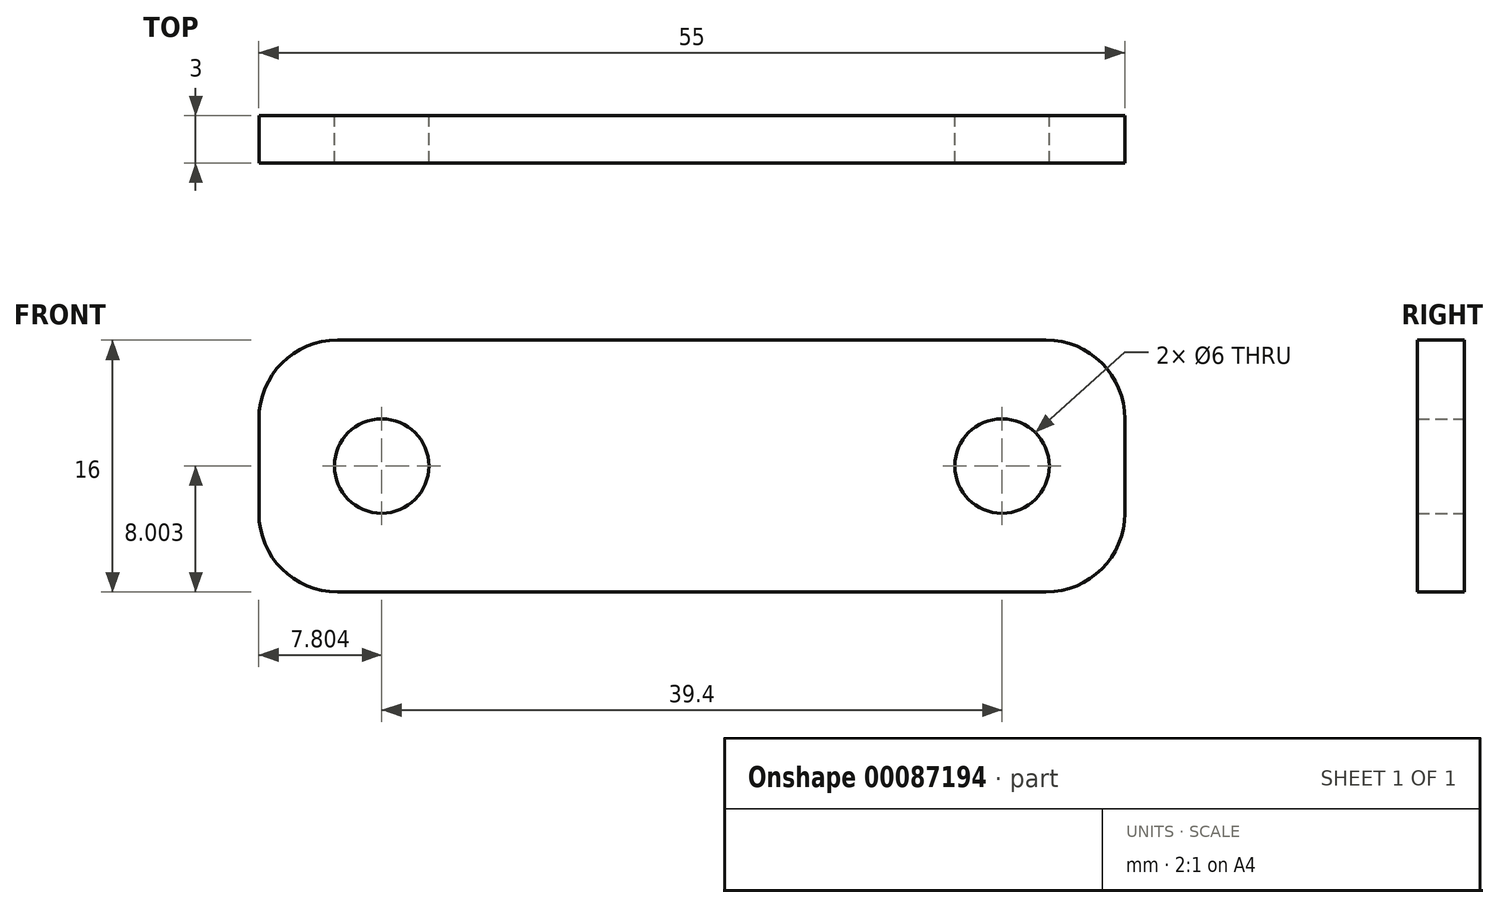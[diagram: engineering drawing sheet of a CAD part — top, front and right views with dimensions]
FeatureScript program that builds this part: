
annotation { "Feature Type Name" : "Feature", "Feature Type Description" : "" }
export const myFeature = defineFeature(function(context is Context, id is Id, definition is map)
    precondition{}
    {
        {
            var Q0;
            Q0=qCreatedBy(makeId("Front.planeOp"),FACE);
            var sketch = newSketch(context, id + "F0", { "sketchPlane" : qUnion([Q0])});
            skLineSegment(sketch, "E0", {"start": v(-167.64, 33.38) * mm, "end": v(-128.24, 33.38) * mm, "construction": true});
            skCircle(sketch, "E1", {"center": v(-167.64, 33.38) * mm, "radius": 3 * mm});
            skCircle(sketch, "E2", {"center": v(-128.24, 33.38) * mm, "radius": 3 * mm});
            skLineSegment(sketch, "E3.bottom", {"start": v(-125.44, 41.38) * mm, "end": v(-170.44, 41.38) * mm});
            skLineSegment(sketch, "E3.top", {"start": v(-125.44, 25.38) * mm, "end": v(-170.44, 25.38) * mm});
            skLineSegment(sketch, "E3.left", {"start": v(-120.44, 36.38) * mm, "end": v(-120.44, 30.38) * mm});
            skLineSegment(sketch, "E3.right", {"start": v(-175.44, 36.38) * mm, "end": v(-175.44, 30.38) * mm});
            skPoint(sketch, "E3.middle", {"position": v(-147.94, 33.38) * mm});
            skPoint(sketch, "E4.visualSharp", {"position": v(-120.44, 41.38) * mm});
            skArc(sketch, "E4.filletArc", {"start": v(-120.44, 36.38) * mm, "mid": v(-121.9, 39.92) * mm, "end": v(-125.44, 41.38) * mm});
            skPoint(sketch, "E5.visualSharp", {"position": v(-120.44, 25.38) * mm});
            skArc(sketch, "E5.filletArc", {"start": v(-125.44, 25.38) * mm, "mid": v(-121.9, 26.85) * mm, "end": v(-120.44, 30.38) * mm});
            skPoint(sketch, "E6.visualSharp", {"position": v(-175.44, 25.38) * mm});
            skArc(sketch, "E6.filletArc", {"start": v(-175.44, 30.38) * mm, "mid": v(-173.97, 26.85) * mm, "end": v(-170.44, 25.38) * mm});
            skPoint(sketch, "E7.visualSharp", {"position": v(-175.44, 41.38) * mm});
            skArc(sketch, "E7.filletArc", {"start": v(-170.44, 41.38) * mm, "mid": v(-173.97, 39.92) * mm, "end": v(-175.44, 36.38) * mm});
            skSolve(sketch);
        }
        {
            var Q0;
            Q0 = qSketchRegion(id + "F0", true);
            extrude(context, id + "F1", {"entities" : qUnion([Q0]), "depth" : 3 * mm});
        }
    });
